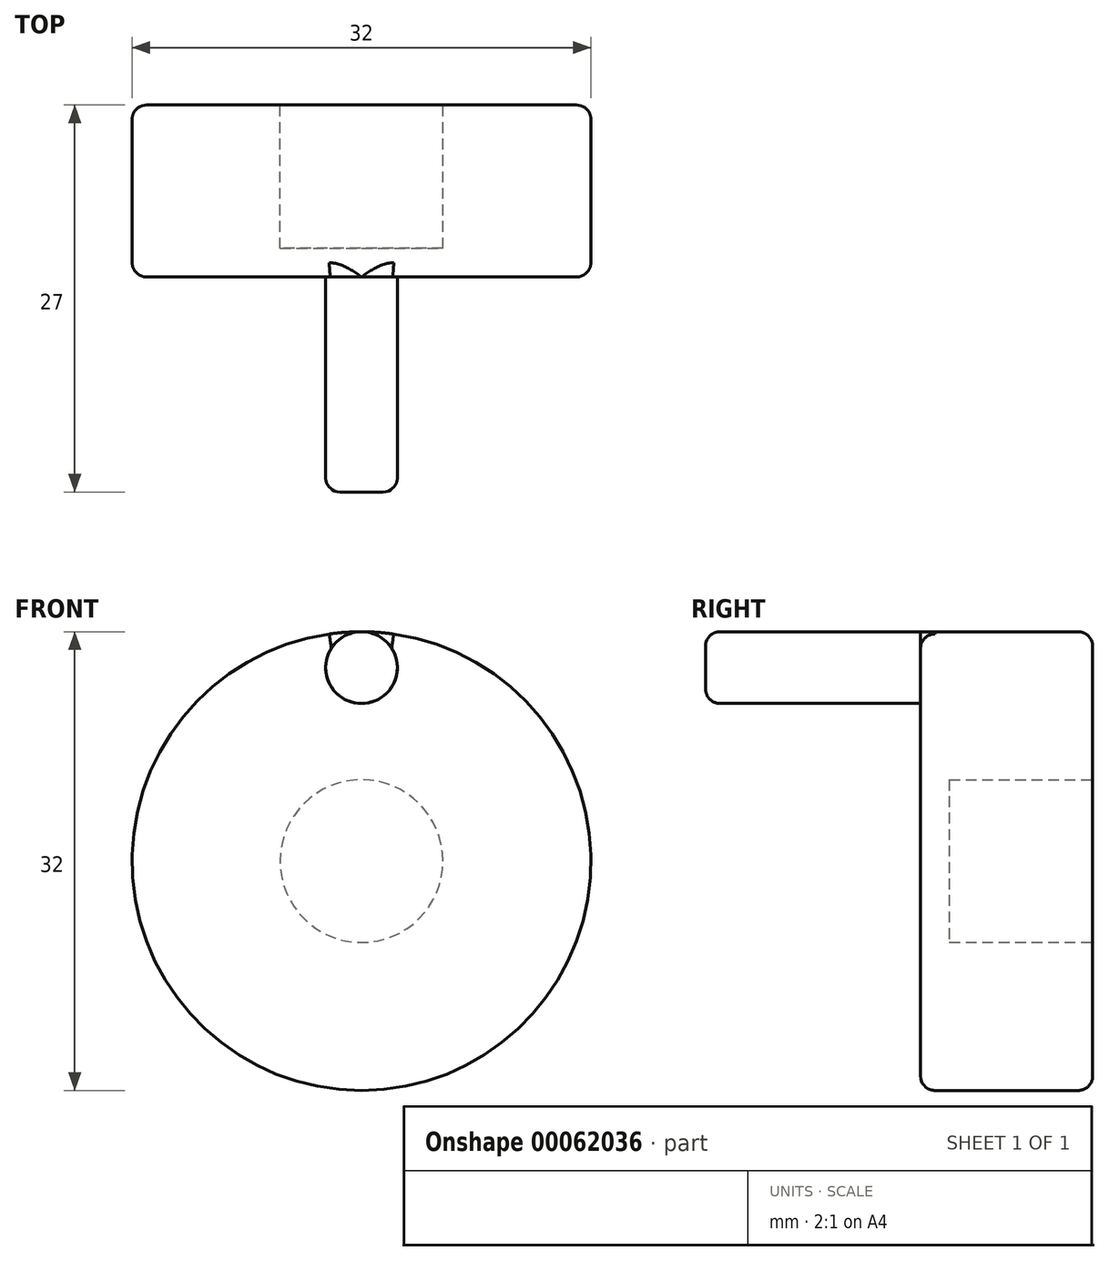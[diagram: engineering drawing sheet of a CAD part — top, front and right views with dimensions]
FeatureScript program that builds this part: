
annotation { "Feature Type Name" : "Feature", "Feature Type Description" : "" }
export const myFeature = defineFeature(function(context is Context, id is Id, definition is map)
    precondition{}
    {
        {
            var Q0;
            Q0=qCreatedBy(makeId("Front.planeOp"),FACE);
            var sketch = newSketch(context, id + "F0", { "sketchPlane" : qUnion([Q0])});
            skCircle(sketch, "E0", {"center": v(0, 0) * mm, "radius": 16 * mm});
            skSolve(sketch);
        }
        {
            var Q0;
            Q0 = qSketchRegion(id + "F0", true);
            extrude(context, id + "F1", {"entities" : qUnion([Q0]), "depth" : 12 * mm});
        }
        {
            var Q0;
            Q0=makeQuery(id+"F1.opExtrude","CAP_FACE",FACE,{"disambiguationData":[OSD([sQuery(id+"F0.wireOp",EDGE,"E0")])],"isStart":false});
            var sketch = newSketch(context, id + "F2", { "sketchPlane" : qUnion([Q0])});
            skCircle(sketch, "E1", {"center": v(0, 13.5) * mm, "radius": 2.5 * mm});
            skSolve(sketch);
        }
        {
            var Q0;
            Q0 = qSketchRegion(id + "F2", true);
            extrude(context, id + "F3", {"entities" : qUnion([Q0]), "operationType" : NewBodyOperationType.ADD, "depth" : 15 * mm});
        }
        {
            var Q0;
            Q0=makeQuery(id+"F1.opExtrude","CAP_FACE",FACE,{"disambiguationData":[OSD([sQuery(id+"F0.wireOp",EDGE,"E0")])],"isStart":true});
            var sketch = newSketch(context, id + "F4", { "sketchPlane" : qUnion([Q0])});
            skCircle(sketch, "E2", {"center": v(0, 0) * mm, "radius": 5.67 * mm});
            skSolve(sketch);
        }
        {
            var Q0;
            Q0 = qSketchRegion(id + "F4", true);
            extrude(context, id + "F5", {"entities" : qUnion([Q0]), "operationType" : NewBodyOperationType.REMOVE, "oppositeDirection" : true, "depth" : 10 * mm});
        }
        {
            var Q0;
            Q0=makeQuery(id+"F3.opExtrude","CAP_EDGE",EDGE,{"disambiguationData":[OSD([sQuery(id+"F2.wireOp",EDGE,"E1")])],"isStart":false});
            fillet(context, id + "F6", {"entities" : qUnion([Q0]), "radius" : 1 * mm, "tangentPropagation" : true, "allowEdgeOverflow" : false});
        }
        {
            var Q0;
            Q0=makeQuery(id+"F3.opExtrude","CAP_EDGE",EDGE,{"disambiguationData":[OSD([sQuery(id+"F2.wireOp",EDGE,"E1")])],"isStart":true});
            var Q1;
            Q1=makeQuery(id+"F1.opExtrude","CAP_EDGE",EDGE,{"disambiguationData":[OSD([sQuery(id+"F0.wireOp",EDGE,"E0")])],"isStart":false});
            fillet(context, id + "F7", {"entities" : qUnion([Q0, Q1]), "radius" : 1 * mm, "tangentPropagation" : true, "allowEdgeOverflow" : false});
        }
        {
            var Q0;
            Q0=makeQuery(id+"F1.opExtrude","CAP_EDGE",EDGE,{"disambiguationData":[OSD([sQuery(id+"F0.wireOp",EDGE,"E0")])],"isStart":true});
            var Q1;
            Q1=makeQuery(id+"F5.boolean.opBoolean","COPY",EDGE,{"derivedFrom":makeQuery(id+"F5.opExtrude","CAP_EDGE",EDGE,{"disambiguationData":[OSD([sQuery(id+"F4.wireOp",EDGE,"E2")])],"isStart":true})});
            fillet(context, id + "F8", {"entities" : qUnion([Q0, Q1]), "radius" : 1 * mm, "tangentPropagation" : true, "allowEdgeOverflow" : false});
        }
    });
